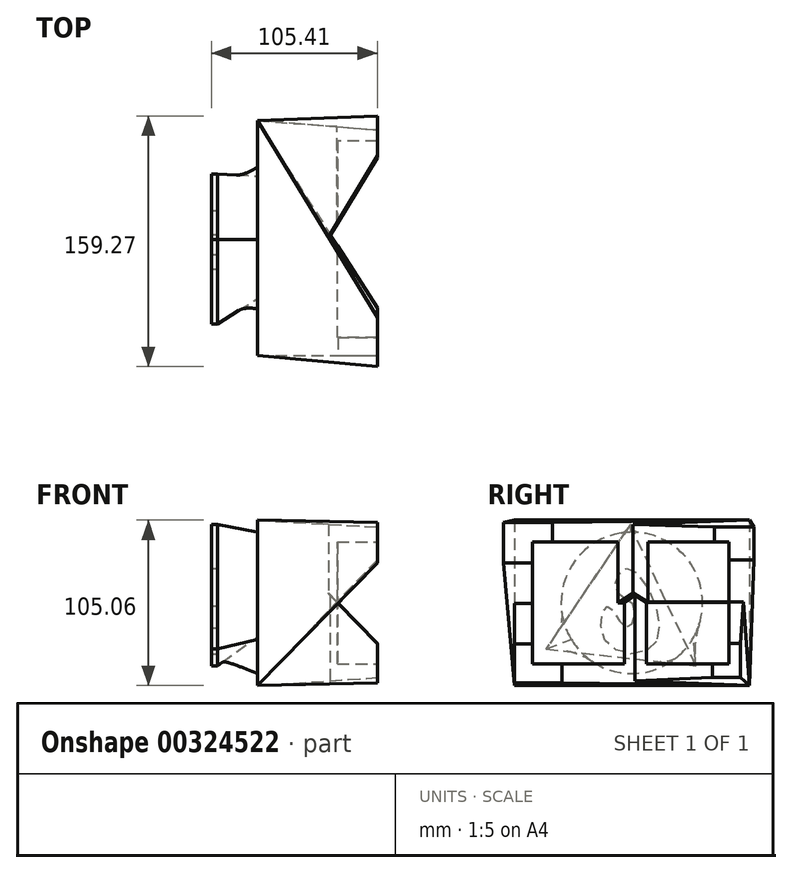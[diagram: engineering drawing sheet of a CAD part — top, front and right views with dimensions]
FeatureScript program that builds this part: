
annotation { "Feature Type Name" : "Feature", "Feature Type Description" : "" }
export const myFeature = defineFeature(function(context is Context, id is Id, definition is map)
    precondition{}
    {
        {
            var Q0;
            Q0=qCreatedBy(makeId("Right.planeOp"),FACE);
            var sketch = newSketch(context, id + "F0", { "sketchPlane" : qUnion([Q0])});
            skLineSegment(sketch, "E0.bottom", {"start": v(-56, 47.66) * mm, "end": v(93.23, 47.66) * mm});
            skLineSegment(sketch, "E0.top", {"start": v(-56, -57.4) * mm, "end": v(93.23, -57.4) * mm});
            skLineSegment(sketch, "E0.left", {"start": v(-56, 47.66) * mm, "end": v(-56, -57.4) * mm});
            skLineSegment(sketch, "E0.right", {"start": v(93.23, 47.66) * mm, "end": v(93.23, -57.4) * mm});
            skSolve(sketch);
        }
        {
            var Q0;
            Q0=qCreatedBy(makeId("Right.planeOp"),FACE);
            cPlane(context, id + "F1", {"entities" : qUnion([Q0]), "cplaneType" : CPlaneType.OFFSET, "offset" : 76.2 * mm, "width" : 152.4 * mm, "height" : 152.4 * mm});
        }
        {
            var Q0;
            Q0=qCreatedBy(id+"F1.planeOp",FACE);
            var sketch = newSketch(context, id + "F2", { "sketchPlane" : qUnion([Q0])});
            skLineSegment(sketch, "E1.bottom", {"start": v(-63, 46.1) * mm, "end": v(-31.9, 46.1) * mm});
            skLineSegment(sketch, "E1.top", {"start": v(-63, 20.55) * mm, "end": v(-31.9, 20.55) * mm});
            skLineSegment(sketch, "E1.left", {"start": v(-63, 46.1) * mm, "end": v(-63, 20.55) * mm});
            skLineSegment(sketch, "E1.right", {"start": v(-31.9, 46.1) * mm, "end": v(-31.9, 20.55) * mm});
            skLineSegment(sketch, "E2.bottom", {"start": v(-56.04, -30.99) * mm, "end": v(-25.86, -30.99) * mm});
            skLineSegment(sketch, "E2.top", {"start": v(-56.04, -55.6) * mm, "end": v(-25.86, -55.6) * mm});
            skLineSegment(sketch, "E2.left", {"start": v(-56.04, -30.99) * mm, "end": v(-56.04, -55.6) * mm});
            skLineSegment(sketch, "E2.right", {"start": v(-25.86, -30.99) * mm, "end": v(-25.86, -55.6) * mm});
            skLineSegment(sketch, "E3.bottom", {"start": v(69.8, -30.52) * mm, "end": v(87.44, -30.52) * mm});
            skLineSegment(sketch, "E3.top", {"start": v(69.8, -52.35) * mm, "end": v(87.44, -52.35) * mm});
            skLineSegment(sketch, "E3.left", {"start": v(69.8, -30.52) * mm, "end": v(69.8, -52.35) * mm});
            skLineSegment(sketch, "E3.right", {"start": v(87.44, -30.52) * mm, "end": v(87.44, -52.35) * mm});
            skLineSegment(sketch, "E4.bottom", {"start": v(71.19, 43.3) * mm, "end": v(96.26, 43.3) * mm});
            skLineSegment(sketch, "E4.top", {"start": v(71.19, 22.41) * mm, "end": v(96.26, 22.41) * mm});
            skLineSegment(sketch, "E4.left", {"start": v(71.19, 43.3) * mm, "end": v(71.19, 22.41) * mm});
            skLineSegment(sketch, "E4.right", {"start": v(96.26, 43.3) * mm, "end": v(96.26, 22.41) * mm});
            skSolve(sketch);
        }
        {
            var Q0;
            Q0=makeQuery(id+"F0.imprint","IMPRINT",FACE,{"disambiguationData":[TD([[makeQuery(id+"F0.imprint","IMPRINT",EDGE,{"derivedFrom":sQuery(id+"F0.wireOp",EDGE,"E0.bottom")}),-1.0]])]});
            var Q1;
            Q1=makeQuery(id+"F2.imprint","IMPRINT",FACE,{"disambiguationData":[TD([[makeQuery(id+"F2.imprint","IMPRINT",EDGE,{"derivedFrom":sQuery(id+"F2.wireOp",EDGE,"E4.bottom")}),-1.0]])]});
            loft(context, id + "F3", {"sheetProfilesArray" : [{ "sheetProfileEntities" : qUnion([Q0]) }, { "sheetProfileEntities" : qUnion([Q1]) }]});
        }
        {
            var Q1;
            Q1=makeQuery(id+"F3.opLoft","CAP_FACE",FACE,{"disambiguationData":[OSD([makeQuery(id+"F0.imprint","IMPRINT",FACE,{"disambiguationData":[TD([[makeQuery(id+"F0.imprint","IMPRINT",EDGE,{"derivedFrom":sQuery(id+"F0.wireOp",EDGE,"E0.bottom")}),-1.0]])]})])],"isStart":true});
            var Q2;
            Q2=makeQuery(id+"F2.imprint","IMPRINT",FACE,{"disambiguationData":[TD([[makeQuery(id+"F2.imprint","IMPRINT",EDGE,{"derivedFrom":sQuery(id+"F2.wireOp",EDGE,"E2.bottom")}),-1.0]])]});
            loft(context, id + "F4", {"operationType" : NewBodyOperationType.ADD, "sheetProfilesArray" : [{ "sheetProfileEntities" : qUnion([Q1]) }, { "sheetProfileEntities" : qUnion([Q2]) }]});
        }
        {
            var Q1;
            Q1=makeQuery(id+"F3.opLoft","CAP_FACE",FACE,{"disambiguationData":[OSD([makeQuery(id+"F0.imprint","IMPRINT",FACE,{"disambiguationData":[TD([[makeQuery(id+"F0.imprint","IMPRINT",EDGE,{"derivedFrom":sQuery(id+"F0.wireOp",EDGE,"E0.bottom")}),-1.0]])]})])],"isStart":true});
            var Q2;
            Q2=makeQuery(id+"F2.imprint","IMPRINT",FACE,{"disambiguationData":[TD([[makeQuery(id+"F2.imprint","IMPRINT",EDGE,{"derivedFrom":sQuery(id+"F2.wireOp",EDGE,"E3.bottom")}),-1.0]])]});
            loft(context, id + "F5", {"operationType" : NewBodyOperationType.ADD, "sheetProfilesArray" : [{ "sheetProfileEntities" : qUnion([Q1]) }, { "sheetProfileEntities" : qUnion([Q2]) }]});
        }
        {
            var Q1;
            Q1=makeQuery(id+"F3.opLoft","CAP_FACE",FACE,{"disambiguationData":[OSD([makeQuery(id+"F0.imprint","IMPRINT",FACE,{"disambiguationData":[TD([[makeQuery(id+"F0.imprint","IMPRINT",EDGE,{"derivedFrom":sQuery(id+"F0.wireOp",EDGE,"E0.bottom")}),-1.0]])]})])],"isStart":true});
            var Q2;
            Q2=makeQuery(id+"F2.imprint","IMPRINT",FACE,{"disambiguationData":[TD([[makeQuery(id+"F2.imprint","IMPRINT",EDGE,{"derivedFrom":sQuery(id+"F2.wireOp",EDGE,"E1.bottom")}),-1.0]])]});
            loft(context, id + "F6", {"operationType" : NewBodyOperationType.ADD, "sheetProfilesArray" : [{ "sheetProfileEntities" : qUnion([Q1]) }, { "sheetProfileEntities" : qUnion([Q2]) }]});
        }
        {
            var Q0;
            Q0=makeQuery(id+"F3.opLoft","CAP_FACE",FACE,{"disambiguationData":[OSD([makeQuery(id+"F0.imprint","IMPRINT",FACE,{"disambiguationData":[TD([[makeQuery(id+"F0.imprint","IMPRINT",EDGE,{"derivedFrom":sQuery(id+"F0.wireOp",EDGE,"E0.bottom")}),-1.0]])]})])],"isStart":true});
            var sketch = newSketch(context, id + "F7", { "sketchPlane" : qUnion([Q0])});
            skPoint(sketch, "E5", {"position": v(56, -4.87) * mm});
            skCircle(sketch, "E6", {"center": v(-18.61, -4.87) * mm, "radius": 44.92 * mm});
            skPoint(sketch, "E6.centerSnap0", {"position": v(-18.61, -57.4) * mm});
            skSolve(sketch);
        }
        {
            var Q0;
            Q0=qCreatedBy(makeId("Right.planeOp"),FACE);
            cPlane(context, id + "F8", {"entities" : qUnion([Q0]), "cplaneType" : CPlaneType.OFFSET, "offset" : 25.4 * mm, "oppositeDirection" : true, "width" : 152.4 * mm, "height" : 152.4 * mm});
        }
        {
            var Q0;
            Q0=qCreatedBy(id+"F8.planeOp",FACE);
            var sketch = newSketch(context, id + "F9", { "sketchPlane" : qUnion([Q0])});
            skLineSegment(sketch, "E7", {"start": v(17.69, 44.88) * mm, "end": v(-35.89, -34.1) * mm});
            skLineSegment(sketch, "E8", {"start": v(-35.89, -34.1) * mm, "end": v(59.43, -44.88) * mm});
            skLineSegment(sketch, "E9", {"start": v(59.43, -44.88) * mm, "end": v(17.69, 44.88) * mm});
            skSolve(sketch);
        }
        {
            var Q1;
            Q1=makeQuery(id+"F9.imprint","IMPRINT",FACE,{"disambiguationData":[TD([[makeQuery(id+"F9.imprint","IMPRINT",EDGE,{"derivedFrom":sQuery(id+"F9.wireOp",EDGE,"E7")}),1.0]])]});
            var Q2;
            Q2=makeQuery(id+"F7.imprint","IMPRINT",FACE,{"disambiguationData":[TD([[makeQuery(id+"F7.imprint","IMPRINT",EDGE,{"derivedFrom":sQuery(id+"F7.wireOp",EDGE,"E6")}),1.0]])]});
            loft(context, id + "F10", {"operationType" : NewBodyOperationType.ADD, "sheetProfilesArray" : [{ "sheetProfileEntities" : qUnion([Q1]) }, { "sheetProfileEntities" : qUnion([Q2]) }]});
        }
        {
            var Q0;
            Q0=qCreatedBy(id+"F1.planeOp",FACE);
            var sketch = newSketch(context, id + "F11", { "sketchPlane" : qUnion([Q0])});
            skLineSegment(sketch, "E10.bottom", {"start": v(-44.58, 33.74) * mm, "end": v(80.3, 33.74) * mm});
            skLineSegment(sketch, "E10.top", {"start": v(-44.58, -43.48) * mm, "end": v(80.3, -43.48) * mm});
            skLineSegment(sketch, "E10.left", {"start": v(-44.58, 33.74) * mm, "end": v(-44.58, -43.48) * mm});
            skLineSegment(sketch, "E10.right", {"start": v(80.3, 33.74) * mm, "end": v(80.3, -43.48) * mm});
            skSolve(sketch);
        }
        {
            var Q0;
            Q0 = qSketchRegion(id + "F11", true);
            extrude(context, id + "F12", {"entities" : qUnion([Q0]), "operationType" : NewBodyOperationType.REMOVE, "oppositeDirection" : true, "depth" : 25.4 * mm});
        }
        {
            var Q0;
            Q0=makeQuery(id+"F10.opLoft","CAP_FACE",FACE,{"disambiguationData":[OSD([makeQuery(id+"F9.imprint","IMPRINT",FACE,{"disambiguationData":[TD([[makeQuery(id+"F9.imprint","IMPRINT",EDGE,{"derivedFrom":sQuery(id+"F9.wireOp",EDGE,"E7")}),1.0]])]})])],"isStart":true});
            var sketch = newSketch(context, id + "F13", { "sketchPlane" : qUnion([Q0])});
            skFitSpline(sketch, "E11", {"points": [v(-34.36, -29.35) * mm, v(-1.93, -29.2) * mm, v(-3.64, -6.94) * mm, v(-14.95, -20.62) * mm, v(-20.37, -7.62) * mm, v(-8.62, 3.18) * mm, v(-16.31, 17.12) * mm, v(-34.36, -29.35) * mm]});
            skSolve(sketch);
        }
        {
            var Q0;
            Q0=makeQuery(id+"F13.imprint","IMPRINT",FACE,{"disambiguationData":[TD([[makeQuery(id+"F13.imprint","IMPRINT",EDGE,{"derivedFrom":sQuery(id+"F13.wireOp",EDGE,"E11")}),-1.0]])]});
            extrude(context, id + "F14", {"entities" : qUnion([Q0]), "operationType" : NewBodyOperationType.ADD, "depth" : 3.8 * mm});
        }
    });
